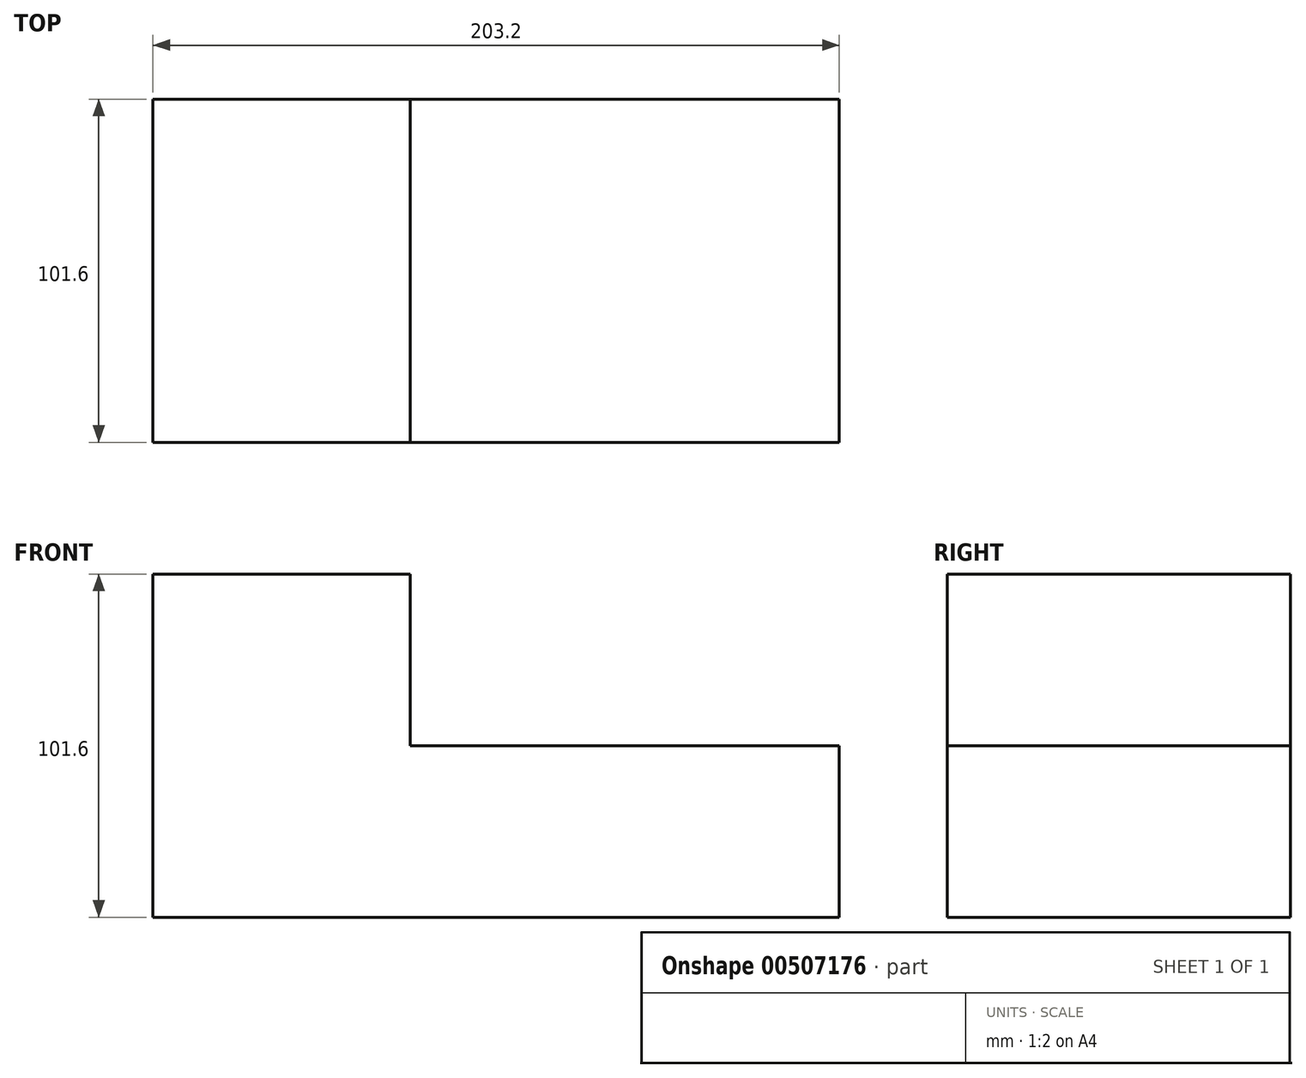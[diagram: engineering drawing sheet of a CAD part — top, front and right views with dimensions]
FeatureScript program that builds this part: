
annotation { "Feature Type Name" : "Feature", "Feature Type Description" : "" }
export const myFeature = defineFeature(function(context is Context, id is Id, definition is map)
    precondition{}
    {
        {
            var Q0;
            Q0=qCreatedBy(makeId("Front.planeOp"),FACE);
            var sketch = newSketch(context, id + "F0", { "sketchPlane" : qUnion([Q0])});
            skLineSegment(sketch, "E0", {"start": v(0, 0) * mm, "end": v(203.2, 0) * mm});
            skLineSegment(sketch, "E1", {"start": v(203.2, 0) * mm, "end": v(203.2, 50.8) * mm});
            skLineSegment(sketch, "E2", {"start": v(76.2, 50.8) * mm, "end": v(203.2, 50.8) * mm});
            skLineSegment(sketch, "E3", {"start": v(76.2, 50.8) * mm, "end": v(76.2, 101.6) * mm});
            skLineSegment(sketch, "E4", {"start": v(0, 101.6) * mm, "end": v(76.2, 101.6) * mm});
            skLineSegment(sketch, "E5", {"start": v(0, 101.6) * mm, "end": v(0, 0) * mm});
            skSolve(sketch);
        }
        {
            var Q0;
            Q0=makeQuery(id+"F0.imprint","IMPRINT",FACE,{"disambiguationData":[TD([[makeQuery(id+"F0.imprint","IMPRINT",EDGE,{"derivedFrom":sQuery(id+"F0.wireOp",EDGE,"E0")}),1.0]])]});
            extrude(context, id + "F1", {"entities" : qUnion([Q0]), "depth" : 101.6 * mm});
        }
    });
